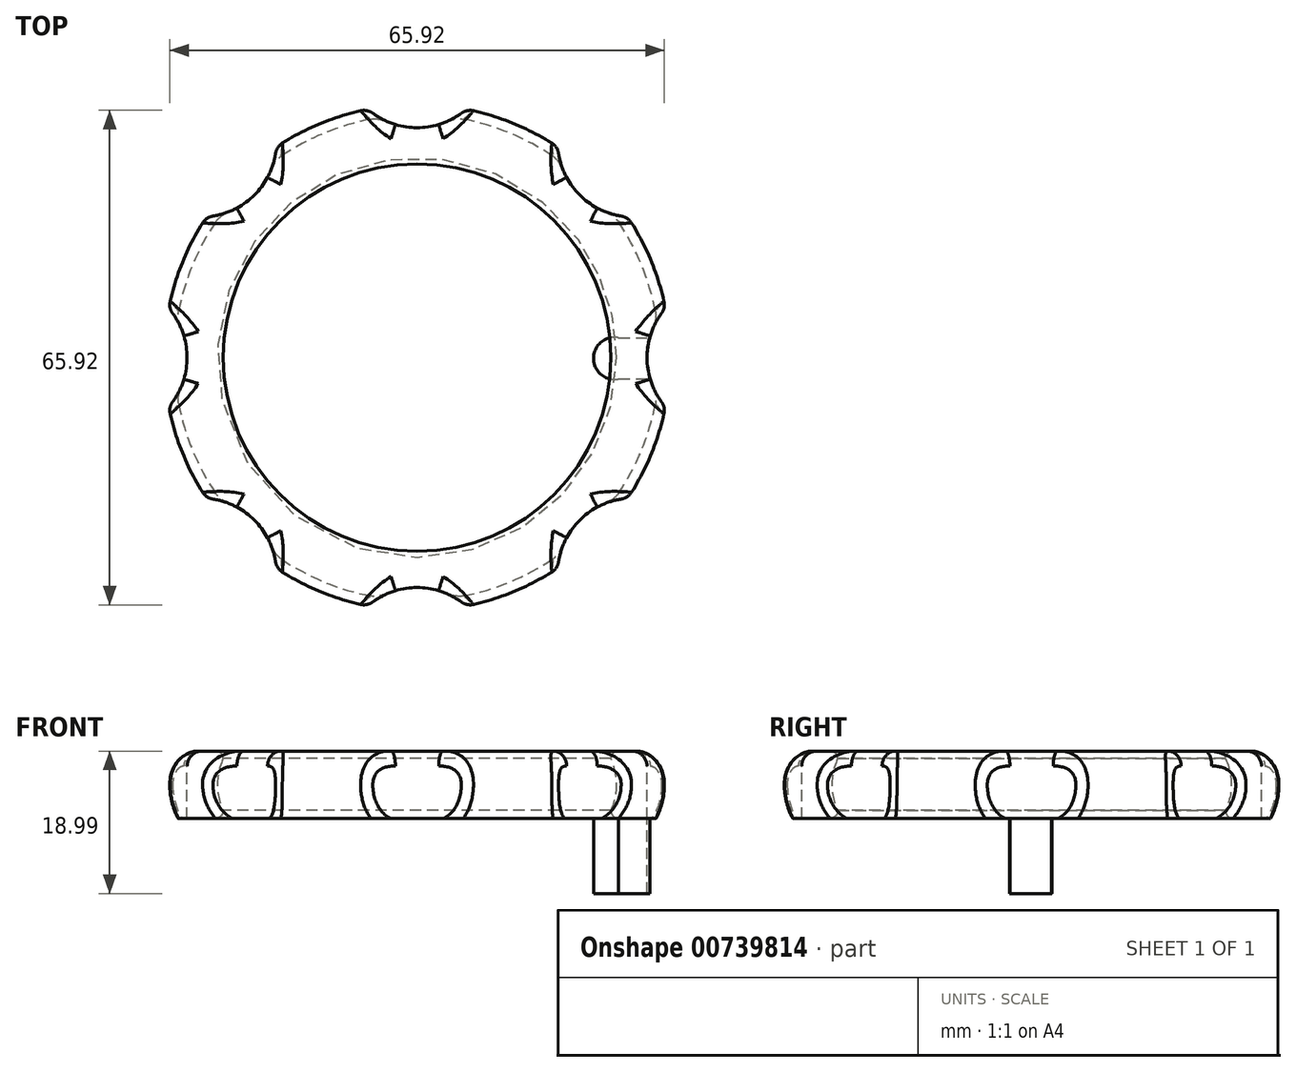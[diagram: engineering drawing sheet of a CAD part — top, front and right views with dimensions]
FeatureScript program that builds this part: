
annotation { "Feature Type Name" : "Feature", "Feature Type Description" : "" }
export const myFeature = defineFeature(function(context is Context, id is Id, definition is map)
    precondition{}
    {
        {
            var Q0;
            Q0=qCreatedBy(makeId("Top.planeOp"),FACE);
            var sketch = newSketch(context, id + "F0", { "sketchPlane" : qUnion([Q0])});
            skCircle(sketch, "E0", {"center": v(0, 0) * mm, "radius": 26 * mm});
            skCircle(sketch, "E1", {"center": v(0, 0) * mm, "radius": 32.5 * mm});
            skSolve(sketch);
        }
        {
            var Q0;
            Q0=qCreatedBy(makeId("Top.planeOp"),FACE);
            cPlane(context, id + "F1", {"entities" : qUnion([Q0]), "cplaneType" : CPlaneType.OFFSET, "offset" : 30 * mm, "width" : 150 * mm, "height" : 150 * mm});
        }
        {
            var Q0;
            Q0=qCreatedBy(id+"F1.planeOp",FACE);
            var sketch = newSketch(context, id + "F2", { "sketchPlane" : qUnion([Q0])});
            skCircle(sketch, "E2", {"center": v(0, 0) * mm, "radius": 26 * mm});
            skCircle(sketch, "E3", {"center": v(0, 0) * mm, "radius": 32.5 * mm});
            skSolve(sketch);
        }
        {
            var Q0;
            Q0=qCreatedBy(makeId("Front.planeOp"),FACE);
            var sketch = newSketch(context, id + "F3", { "sketchPlane" : qUnion([Q0])});
            skLineSegment(sketch, "E4", {"start": v(50.15, 15) * mm, "end": v(50.15, 11) * mm, "construction": true});
            skLineSegment(sketch, "E5", {"start": v(50.15, 11) * mm, "end": v(12.79, 11) * mm, "construction": true});
            skLineSegment(sketch, "E6", {"start": v(12.79, 11) * mm, "end": v(12.79, 7) * mm, "construction": true});
            skLineSegment(sketch, "E7", {"start": v(12.79, 7) * mm, "end": v(50.15, 7) * mm, "construction": true});
            skLineSegment(sketch, "E8", {"start": v(50.15, 7) * mm, "end": v(50.15, 3) * mm, "construction": true});
            skLineSegment(sketch, "E9", {"start": v(50.15, 3) * mm, "end": v(13.06, 3) * mm, "construction": true});
            skLineSegment(sketch, "E10", {"start": v(13.06, 3) * mm, "end": v(13.06, 0) * mm, "construction": true});
            skLineSegment(sketch, "E11", {"start": v(13.06, 0) * mm, "end": v(50.15, 0) * mm, "construction": true});
            skArc(sketch, "E12", {"start": v(26.32, 15) * mm, "mid": v(24.95, 13) * mm, "end": v(26.32, 11) * mm});
            skArc(sketch, "E13", {"start": v(26.32, 11) * mm, "mid": v(24.9, 9) * mm, "end": v(26.32, 7) * mm});
            skArc(sketch, "E14", {"start": v(26.32, 7) * mm, "mid": v(24.9, 5) * mm, "end": v(26.32, 3) * mm});
            skArc(sketch, "E15", {"start": v(26.32, 3) * mm, "mid": v(24.9, 1.5) * mm, "end": v(26.32, 0) * mm});
            skLineSegment(sketch, "E16", {"start": v(26.32, 0) * mm, "end": v(32.33, 0) * mm});
            skLineSegment(sketch, "E17", {"start": v(25, 30.36) * mm, "end": v(24.9, -1.2) * mm, "construction": true});
            skPoint(sketch, "E17.endSnap0", {"position": v(24.9, 1.5) * mm});
            skArc(sketch, "E18", {"start": v(32.33, 0) * mm, "mid": v(34.33, 7.5) * mm, "end": v(32.33, 15) * mm});
            skLineSegment(sketch, "E19", {"start": v(26.32, 15) * mm, "end": v(32.33, 15) * mm});
            skPoint(sketch, "E20.orphan", {"position": v(32.32, 30) * mm});
            skSolve(sketch);
        }
        {
            var Q0;
            Q0=makeQuery(id+"F3.imprint","IMPRINT",FACE,{"disambiguationData":[TD([[makeQuery(id+"F3.imprint","IMPRINT",EDGE,{"derivedFrom":sQuery(id+"F3.wireOp",EDGE,"40ogjAE2-JOZK-r5aG-7V21-pRMZDkrU9Inz")}),1.0]])]});
            var Q1;
            Q1=sQuery(id+"F3.wireOp",EDGE,"E19");
            var Q2;
            Q2=sQuery(id+"F3.wireOp",EDGE,"E12");
            var Q3;
            Q3=sQuery(id+"F3.wireOp",EDGE,"E13");
            var Q4;
            Q4=sQuery(id+"F3.wireOp",EDGE,"E14");
            var Q5;
            Q5=sQuery(id+"F3.wireOp",EDGE,"E15");
            var Q6;
            Q6=sQuery(id+"F3.wireOp",EDGE,"E16");
            var Q7;
            Q7=sQuery(id+"F3.wireOp",EDGE,"E18");
            var Q8;
            Q8=sQuery(id+"F2.wireOp",EDGE,"E2");
            sweep(context, id + "F4", {"bodyType" : ExtendedToolBodyType.SURFACE, "profiles" : qUnion([Q0]), "surfaceProfiles" : qUnion([Q1, Q2, Q3, Q4, Q5, Q6, Q7]), "path" : qUnion([Q8])});
        }
        {
            var Q0;
            Q0=qCreatedBy(makeId("Front.planeOp"),FACE);
            var sketch = newSketch(context, id + "F5", { "sketchPlane" : qUnion([Q0])});
            skLineSegment(sketch, "E21", {"start": v(25.83, 8) * mm, "end": v(25.83, 1.08) * mm});
            skLineSegment(sketch, "E22", {"start": v(26.91, 0) * mm, "end": v(32.38, 0) * mm});
            skLineSegment(sketch, "E23", {"start": v(26.83, 9) * mm, "end": v(29.37, 9) * mm});
            skArc(sketch, "E24", {"start": v(32.38, 0) * mm, "mid": v(33.44, 2.26) * mm, "end": v(33.76, 4.73) * mm});
            skPoint(sketch, "E25.visualSharp", {"position": v(25.83, 9) * mm});
            skArc(sketch, "E25.filletArc", {"start": v(26.83, 9) * mm, "mid": v(26.13, 8.7) * mm, "end": v(25.83, 8) * mm});
            skPoint(sketch, "E26.visualSharp", {"position": v(32.38, 9) * mm});
            skArc(sketch, "E26.filletArc", {"start": v(33.76, 4.73) * mm, "mid": v(32.43, 7.75) * mm, "end": v(29.37, 9) * mm});
            skPoint(sketch, "E27.visualSharp", {"position": v(25.83, 0) * mm});
            skArc(sketch, "E27.filletArc", {"start": v(25.83, 1.08) * mm, "mid": v(26.15, 0.32) * mm, "end": v(26.91, 0) * mm});
            skArc(sketch, "E28", {"start": v(25.83, 1.08) * mm, "mid": v(26.62, 4.54) * mm, "end": v(25.83, 8) * mm});
            skSolve(sketch);
        }
        {
            var Q0;
            Q0=makeQuery(id+"F5.imprint","IMPRINT",FACE,{"disambiguationData":[TD([[makeQuery(id+"F5.imprint","IMPRINT",EDGE,{"derivedFrom":sQuery(id+"F5.wireOp",EDGE,"E22")}),1.0]])]});
            var Q1;
            Q1=sQuery(id+"F2.wireOp",EDGE,"E2");
            sweep(context, id + "F6", {"profiles" : qUnion([Q0]), "path" : qUnion([Q1])});
        }
        {
            var Q0;
            Q0=qCreatedBy(makeId("Top.planeOp"),FACE);
            var sketch = newSketch(context, id + "F8", { "sketchPlane" : qUnion([Q0])});
            skLineSegment(sketch, "E29.bottom", {"start": v(26.88, -2.85) * mm, "end": v(32.38, -2.85) * mm});
            skLineSegment(sketch, "E29.top", {"start": v(26.88, 2.65) * mm, "end": v(32.38, 2.65) * mm});
            skLineSegment(sketch, "E29.left", {"start": v(26.88, -2.85) * mm, "end": v(26.88, 2.65) * mm});
            skLineSegment(sketch, "E29.right", {"start": v(32.38, -2.85) * mm, "end": v(32.38, 2.65) * mm});
            skArc(sketch, "E30", {"start": v(26.88, 2.65) * mm, "mid": v(23.52, -0.1) * mm, "end": v(26.88, -2.85) * mm});
            skSolve(sketch);
        }
        {
            var Q0;
            Q0 = qSketchRegion(id + "F8", true);
            extrude(context, id + "F9", {"entities" : qUnion([Q0]), "oppositeDirection" : true, "depth" : 10 * mm, "offsetDistance" : 25 * mm});
        }
        {
            var Q0;
            Q0=qCreatedBy(makeId("Top.planeOp"),FACE);
            var sketch = newSketch(context, id + "F11", { "sketchPlane" : qUnion([Q0])});
            skCircle(sketch, "E31", {"center": v(0, 40.65) * mm, "radius": 10 * mm});
            skCircle(sketch, "E32.1.0", {"center": v(28.75, 28.75) * mm, "radius": 10 * mm});
            skCircle(sketch, "E32.2.0", {"center": v(40.65, 0) * mm, "radius": 10 * mm});
            skCircle(sketch, "E32.3.0", {"center": v(28.75, -28.75) * mm, "radius": 10 * mm});
            skCircle(sketch, "E32.4.0", {"center": v(0, -40.65) * mm, "radius": 10 * mm});
            skCircle(sketch, "E32.5.0", {"center": v(-28.75, -28.75) * mm, "radius": 10 * mm});
            skCircle(sketch, "E32.6.0", {"center": v(-40.65, 0) * mm, "radius": 10 * mm});
            skCircle(sketch, "E32.7.0", {"center": v(-28.75, 28.75) * mm, "radius": 10 * mm});
            skPoint(sketch, "E32.center", {"position": v(0, 0) * mm});
            skLineSegment(sketch, "E32.anchor1", {"start": v(0, 0) * mm, "end": v(0, 40.65) * mm, "construction": true});
            skLineSegment(sketch, "E32.anchor2", {"start": v(0, 0) * mm, "end": v(-28.75, 28.75) * mm, "construction": true});
            skSolve(sketch);
        }
        {
            var Q0;
            Q0 = qSketchRegion(id + "F11", true);
            extrude(context, id + "F12", {"entities" : qUnion([Q0]), "operationType" : NewBodyOperationType.REMOVE, "oppositeDirection" : true, "depth" : 25 * mm, "offsetDistance" : 25 * mm, "hasSecondDirection" : true, "secondDirectionOppositeDirection" : false, "secondDirectionDepth" : 25 * mm});
        }
        {
            var Q0;
            Q0=makeQuery(id+"F12.boolean.opBoolean","INTERSECT",EDGE,{"derivedFrom":[makeQuery(id+"F6.opSweep","SWEPT_FACE",FACE,{"disambiguationData":[OSD([sQuery(id+"F2.wireOp",EDGE,"E2"),sQuery(id+"F5.wireOp",EDGE,"E26.filletArc")])]}),makeQuery(id+"F12.opExtrude","SWEPT_FACE",FACE,{"disambiguationData":[OSD([sQuery(id+"F11.wireOp",EDGE,"E32.5.0")])]})]});
            var Q1;
            Q1=makeQuery(id+"F12.boolean.opBoolean","INTERSECT",EDGE,{"derivedFrom":[makeQuery(id+"F6.opSweep","SWEPT_FACE",FACE,{"disambiguationData":[OSD([sQuery(id+"F2.wireOp",EDGE,"E2"),sQuery(id+"F5.wireOp",EDGE,"E26.filletArc")])]}),makeQuery(id+"F12.opExtrude","SWEPT_FACE",FACE,{"disambiguationData":[OSD([sQuery(id+"F11.wireOp",EDGE,"E32.6.0")])]})]});
            var Q2;
            Q2=makeQuery(id+"F12.boolean.opBoolean","INTERSECT",EDGE,{"derivedFrom":[makeQuery(id+"F6.opSweep","SWEPT_FACE",FACE,{"disambiguationData":[OSD([sQuery(id+"F2.wireOp",EDGE,"E2"),sQuery(id+"F5.wireOp",EDGE,"E26.filletArc")])]}),makeQuery(id+"F12.opExtrude","SWEPT_FACE",FACE,{"disambiguationData":[OSD([sQuery(id+"F11.wireOp",EDGE,"E32.4.0")])]})]});
            var Q3;
            Q3=makeQuery(id+"F12.boolean.opBoolean","INTERSECT",EDGE,{"derivedFrom":[makeQuery(id+"F6.opSweep","SWEPT_FACE",FACE,{"disambiguationData":[OSD([sQuery(id+"F2.wireOp",EDGE,"E2"),sQuery(id+"F5.wireOp",EDGE,"E26.filletArc")])]}),makeQuery(id+"F12.opExtrude","SWEPT_FACE",FACE,{"disambiguationData":[OSD([sQuery(id+"F11.wireOp",EDGE,"E32.3.0")])]})]});
            var Q4;
            Q4=makeQuery(id+"F12.boolean.opBoolean","INTERSECT",EDGE,{"derivedFrom":[makeQuery(id+"F6.opSweep","SWEPT_FACE",FACE,{"disambiguationData":[OSD([sQuery(id+"F2.wireOp",EDGE,"E2"),sQuery(id+"F5.wireOp",EDGE,"E26.filletArc")])]}),makeQuery(id+"F12.opExtrude","SWEPT_FACE",FACE,{"disambiguationData":[OSD([sQuery(id+"F11.wireOp",EDGE,"E32.2.0")])]})]});
            var Q5;
            Q5=makeQuery(id+"F12.boolean.opBoolean","INTERSECT",EDGE,{"derivedFrom":[makeQuery(id+"F6.opSweep","SWEPT_FACE",FACE,{"disambiguationData":[OSD([sQuery(id+"F2.wireOp",EDGE,"E2"),sQuery(id+"F5.wireOp",EDGE,"E26.filletArc")])]}),makeQuery(id+"F12.opExtrude","SWEPT_FACE",FACE,{"disambiguationData":[OSD([sQuery(id+"F11.wireOp",EDGE,"E32.1.0")])]})]});
            var Q6;
            Q6=makeQuery(id+"F12.boolean.opBoolean","INTERSECT",EDGE,{"derivedFrom":[makeQuery(id+"F6.opSweep","SWEPT_FACE",FACE,{"disambiguationData":[OSD([sQuery(id+"F2.wireOp",EDGE,"E2"),sQuery(id+"F5.wireOp",EDGE,"E26.filletArc")])]}),makeQuery(id+"F12.opExtrude","SWEPT_FACE",FACE,{"disambiguationData":[OSD([sQuery(id+"F11.wireOp",EDGE,"E31")])]})]});
            var Q7;
            Q7=makeQuery(id+"F12.boolean.opBoolean","INTERSECT",EDGE,{"derivedFrom":[makeQuery(id+"F6.opSweep","SWEPT_FACE",FACE,{"disambiguationData":[OSD([sQuery(id+"F2.wireOp",EDGE,"E2"),sQuery(id+"F5.wireOp",EDGE,"E26.filletArc")])]}),makeQuery(id+"F12.opExtrude","SWEPT_FACE",FACE,{"disambiguationData":[OSD([sQuery(id+"F11.wireOp",EDGE,"E32.7.0")])]})]});
            fillet(context, id + "F13", {"entities" : qUnion([Q0, Q1, Q2, Q3, Q4, Q5, Q6, Q7]), "radius" : 2 * mm, "tangentPropagation" : true, "allowEdgeOverflow" : false});
        }
    });
